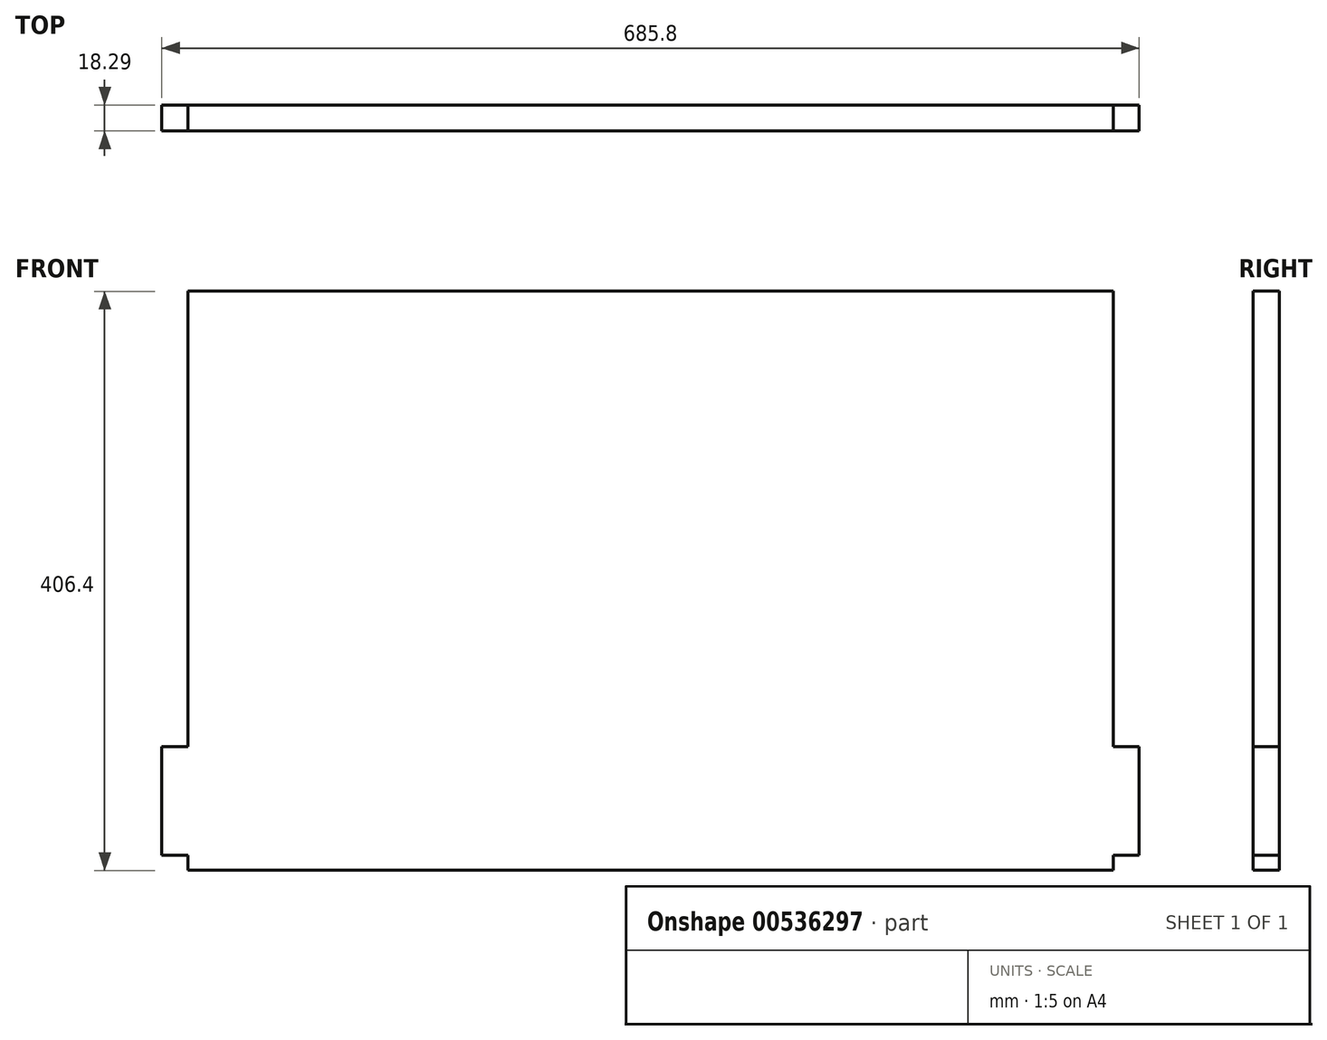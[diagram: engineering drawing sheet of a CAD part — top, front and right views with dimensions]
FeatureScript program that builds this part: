
annotation { "Feature Type Name" : "Feature", "Feature Type Description" : "" }
export const myFeature = defineFeature(function(context is Context, id is Id, definition is map)
    precondition{}
    {
        {
            var Q0;
            Q0=qCreatedBy(makeId("Front.planeOp"),FACE);
            var sketch = newSketch(context, id + "F0", { "sketchPlane" : qUnion([Q0])});
            skLineSegment(sketch, "E0", {"start": v(-47.5, 379.27) * mm, "end": v(601.72, 379.27) * mm});
            skLineSegment(sketch, "E1", {"start": v(601.72, -27.13) * mm, "end": v(-47.5, -27.13) * mm});
            skLineSegment(sketch, "E2", {"start": v(-47.5, -27.13) * mm, "end": v(-47.5, 379.27) * mm});
            skLineSegment(sketch, "E3", {"start": v(601.72, 379.27) * mm, "end": v(601.72, -27.13) * mm});
            skLineSegment(sketch, "E4", {"start": v(-47.5, 59.73) * mm, "end": v(-65.79, 59.73) * mm});
            skLineSegment(sketch, "E5", {"start": v(-65.79, 59.73) * mm, "end": v(-65.79, -16.47) * mm});
            skLineSegment(sketch, "E6", {"start": v(-65.79, -16.47) * mm, "end": v(-47.5, -16.47) * mm});
            skLineSegment(sketch, "E7", {"start": v(601.72, 59.73) * mm, "end": v(620.01, 59.73) * mm});
            skLineSegment(sketch, "E8", {"start": v(620.01, 59.73) * mm, "end": v(620.01, -16.47) * mm});
            skLineSegment(sketch, "E9", {"start": v(620.01, -16.47) * mm, "end": v(601.72, -16.47) * mm});
            skLineSegment(sketch, "E10", {"start": v(-65.79, 21.63) * mm, "end": v(-65.79, -5.5) * mm});
            skLineSegment(sketch, "E11", {"start": v(-65.79, -5.5) * mm, "end": v(-65.79, 21.63) * mm});
            skLineSegment(sketch, "E12", {"start": v(-93.24, -5.5) * mm, "end": v(-92.8, -8.42) * mm});
            skSolve(sketch);
        }
        {
            var Q0;
            Q0 = qSketchRegion(id + "F0", true);
            extrude(context, id + "F1", {"entities" : qUnion([Q0]), "depth" : 18.29 * mm, "offsetDistance" : 25.4 * mm});
        }
    });
